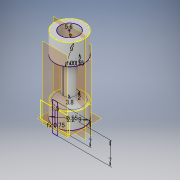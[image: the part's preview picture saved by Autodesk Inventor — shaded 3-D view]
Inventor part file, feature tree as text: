
AUTODESK INVENTOR PART (.ipt)
format: ipt  version: 2019.3 (Build 233278000, 278)  size: 189,952 bytes
history: native  units: in
note: dims shown in document units (in); Inventor stores cm internally (conversion verified against a paired STEP export)
features: sketch x6, extrude x6, other x4, projected_geometry x3, fillet x1
ambient origin geometry x8: Origin, YZ Plane, XZ Plane, XY Plane, X Axis, Y Axis, Z Axis, Center Point
bodies: Body1 (feature_tree)
feature tree (20):
  other  "ソリッド1"
  sketch  "スケッチ2"
  sketch  "スケッチ1"
  extrude  "押し出し1"  Depth=0.0866in
  extrude  "押し出し2"  Depth=0.0217in
  other  "作業平面2"
  sketch  "スケッチ4"
  sketch  "スケッチ3"
  extrude  "押し出し6"  Depth=0.1969in TaperAngle=0.0deg
  other  "作業平面3"
  sketch  "スケッチ5"
  extrude  "押し出し8"  Depth=0.1181in TaperAngle=0.0deg
  sketch  "スケッチ7"
  extrude  "押し出し9"  Depth=0.3543in
  other  "作業平面4"
  extrude  "押し出し10"  Depth=0.1496in
  fillet  "フィレット3"  Radius=0.2756in
  projected_geometry  "投影ループ1"
  projected_geometry  "投影ループ2"
  projected_geometry  "投影ループ3"
